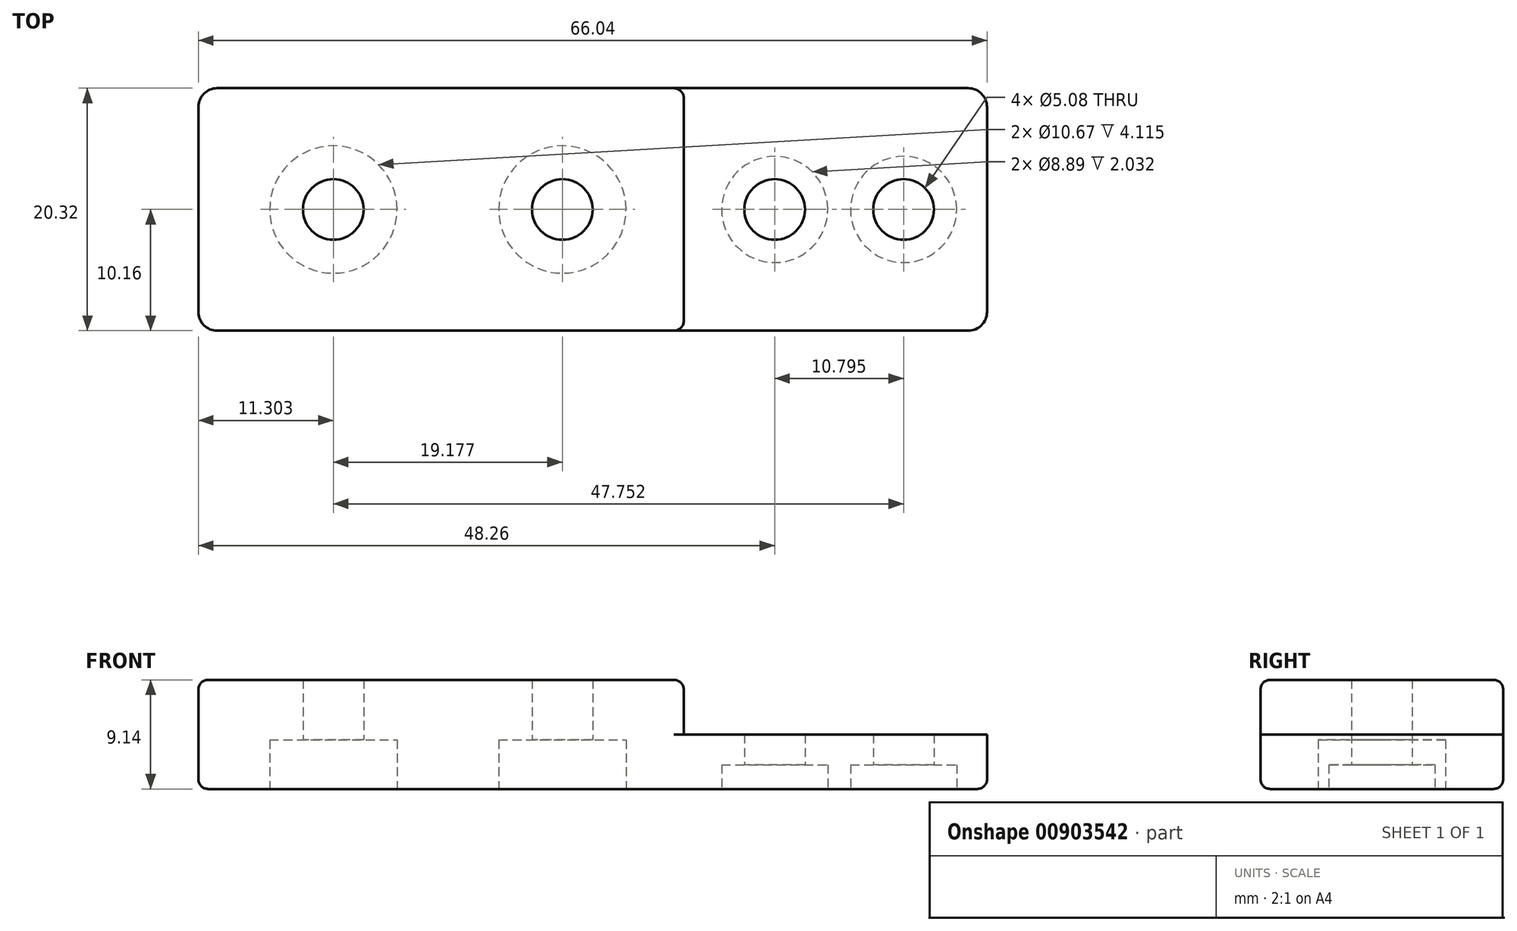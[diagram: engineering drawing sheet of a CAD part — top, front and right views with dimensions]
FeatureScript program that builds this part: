
annotation { "Feature Type Name" : "Feature", "Feature Type Description" : "" }
export const myFeature = defineFeature(function(context is Context, id is Id, definition is map)
    precondition{}
    {
        {
            var Q0;
            Q0=qCreatedBy(makeId("Top.planeOp"),FACE);
            var sketch = newSketch(context, id + "F0", { "sketchPlane" : qUnion([Q0])});
            skLineSegment(sketch, "E0.bottom", {"start": v(-40.64, 10.16) * mm, "end": v(0, 10.16) * mm});
            skLineSegment(sketch, "E0.top", {"start": v(-40.64, -10.16) * mm, "end": v(0, -10.16) * mm});
            skLineSegment(sketch, "E0.left", {"start": v(-40.64, 10.16) * mm, "end": v(-40.64, -10.16) * mm});
            skLineSegment(sketch, "E0.right", {"start": v(0, 10.16) * mm, "end": v(0, -10.16) * mm});
            skCircle(sketch, "E1", {"center": v(-29.34, 0) * mm, "radius": 2.54 * mm});
            skCircle(sketch, "E2", {"center": v(-10.16, 0) * mm, "radius": 2.54 * mm});
            skSolve(sketch);
        }
        {
            var Q0;
            Q0 = qSketchRegion(id + "F0", true);
            extrude(context, id + "F1", {"entities" : qUnion([Q0]), "depth" : 9.14 * mm, "offsetDistance" : 25.4 * mm});
        }
        {
            var Q0;
            Q0=qCreatedBy(makeId("Top.planeOp"),FACE);
            var sketch = newSketch(context, id + "F2", { "sketchPlane" : qUnion([Q0])});
            skLineSegment(sketch, "E3.bottom", {"start": v(0, 10.16) * mm, "end": v(25.4, 10.16) * mm});
            skLineSegment(sketch, "E3.top", {"start": v(0, -10.16) * mm, "end": v(25.4, -10.16) * mm});
            skLineSegment(sketch, "E3.left", {"start": v(0, 10.16) * mm, "end": v(0, -10.16) * mm});
            skLineSegment(sketch, "E3.right", {"start": v(25.4, 10.16) * mm, "end": v(25.4, -10.16) * mm});
            skCircle(sketch, "E4", {"center": v(7.62, 0) * mm, "radius": 2.54 * mm});
            skCircle(sketch, "E5", {"center": v(18.41, 0) * mm, "radius": 2.54 * mm});
            skSolve(sketch);
        }
        {
            var Q0;
            Q0 = qSketchRegion(id + "F2", true);
            extrude(context, id + "F3", {"entities" : qUnion([Q0]), "operationType" : NewBodyOperationType.ADD, "depth" : 4.57 * mm, "offsetDistance" : 25.4 * mm});
        }
        {
            var Q0;
            Q0=makeQuery(id+"F3.boolean.opBoolean","MERGE",FACE,{"derivedFrom":[makeQuery(id+"F1.opExtrude","CAP_FACE",FACE,{"disambiguationData":[OSD([sQuery(id+"F0.wireOp",EDGE,"E0.bottom"),sQuery(id+"F0.wireOp",EDGE,"E0.top"),sQuery(id+"F0.wireOp",EDGE,"E0.left"),sQuery(id+"F0.wireOp",EDGE,"E0.right"),sQuery(id+"F0.wireOp",EDGE,"E1"),sQuery(id+"F0.wireOp",EDGE,"E2")])],"isStart":true}),makeQuery(id+"F3.opExtrude","CAP_FACE",FACE,{"disambiguationData":[OSD([sQuery(id+"F2.wireOp",EDGE,"E3.bottom"),sQuery(id+"F2.wireOp",EDGE,"E3.top"),sQuery(id+"F2.wireOp",EDGE,"E3.left"),sQuery(id+"F2.wireOp",EDGE,"E3.right"),sQuery(id+"F2.wireOp",EDGE,"E4"),sQuery(id+"F2.wireOp",EDGE,"E5")])],"isStart":true})]});
            var sketch = newSketch(context, id + "F4", { "sketchPlane" : qUnion([Q0])});
            skCircle(sketch, "E6", {"center": v(-29.34, 0) * mm, "radius": 5.33 * mm});
            skCircle(sketch, "E7", {"center": v(-10.16, 0) * mm, "radius": 5.33 * mm});
            skCircle(sketch, "E8", {"center": v(-29.34, 0) * mm, "radius": 2.54 * mm});
            skCircle(sketch, "E9", {"center": v(-10.16, 0) * mm, "radius": 2.54 * mm});
            skSolve(sketch);
        }
        {
            var Q0;
            Q0 = qSketchRegion(id + "F4", true);
            extrude(context, id + "F5", {"entities" : qUnion([Q0]), "operationType" : NewBodyOperationType.REMOVE, "oppositeDirection" : true, "depth" : 4.11 * mm, "offsetDistance" : 25.4 * mm});
        }
        {
            var Q0;
            Q0=makeQuery(id+"F3.boolean.opBoolean","MERGE",FACE,{"derivedFrom":[makeQuery(id+"F1.opExtrude","CAP_FACE",FACE,{"disambiguationData":[OSD([sQuery(id+"F0.wireOp",EDGE,"E0.bottom"),sQuery(id+"F0.wireOp",EDGE,"E0.top"),sQuery(id+"F0.wireOp",EDGE,"E0.left"),sQuery(id+"F0.wireOp",EDGE,"E0.right"),sQuery(id+"F0.wireOp",EDGE,"E1"),sQuery(id+"F0.wireOp",EDGE,"E2")])],"isStart":true}),makeQuery(id+"F3.opExtrude","CAP_FACE",FACE,{"disambiguationData":[OSD([sQuery(id+"F2.wireOp",EDGE,"E3.bottom"),sQuery(id+"F2.wireOp",EDGE,"E3.top"),sQuery(id+"F2.wireOp",EDGE,"E3.left"),sQuery(id+"F2.wireOp",EDGE,"E3.right"),sQuery(id+"F2.wireOp",EDGE,"E4"),sQuery(id+"F2.wireOp",EDGE,"E5")])],"isStart":true})]});
            var sketch = newSketch(context, id + "F6", { "sketchPlane" : qUnion([Q0])});
            skCircle(sketch, "E10", {"center": v(7.62, 0) * mm, "radius": 4.45 * mm});
            skCircle(sketch, "E11", {"center": v(18.41, 0) * mm, "radius": 4.45 * mm});
            skCircle(sketch, "E12", {"center": v(7.62, 0) * mm, "radius": 2.54 * mm});
            skCircle(sketch, "E13", {"center": v(18.41, 0) * mm, "radius": 2.54 * mm});
            skSolve(sketch);
        }
        {
            var Q0;
            Q0 = qSketchRegion(id + "F6", true);
            extrude(context, id + "F7", {"entities" : qUnion([Q0]), "operationType" : NewBodyOperationType.REMOVE, "oppositeDirection" : true, "depth" : 2.03 * mm, "offsetDistance" : 25.4 * mm});
        }
        {
            var Q0;
            Q0=makeQuery(id+"F1.opExtrude","SWEPT_EDGE",EDGE,{"disambiguationData":[OSD([sQuery(id+"F0.wireOp",EDGE,"E0.bottom"),sQuery(id+"F0.wireOp",EDGE,"E0.left")])]});
            var Q1;
            Q1=makeQuery(id+"F1.opExtrude","SWEPT_EDGE",EDGE,{"disambiguationData":[OSD([sQuery(id+"F0.wireOp",EDGE,"E0.top"),sQuery(id+"F0.wireOp",EDGE,"E0.left")])]});
            var Q2;
            Q2=makeQuery(id+"F3.opExtrude","SWEPT_EDGE",EDGE,{"disambiguationData":[OSD([sQuery(id+"F2.wireOp",EDGE,"E3.bottom"),sQuery(id+"F2.wireOp",EDGE,"E3.right")])]});
            var Q3;
            Q3=makeQuery(id+"F3.opExtrude","SWEPT_EDGE",EDGE,{"disambiguationData":[OSD([sQuery(id+"F2.wireOp",EDGE,"E3.top"),sQuery(id+"F2.wireOp",EDGE,"E3.right")])]});
            fillet(context, id + "F8", {"entities" : qUnion([Q0, Q1, Q2, Q3]), "radius" : 1.57 * mm, "tangentPropagation" : true, "allowEdgeOverflow" : false});
        }
        {
            var Q0;
            Q0=makeQuery(id+"F3.opExtrude","CAP_EDGE",EDGE,{"disambiguationData":[OSD([sQuery(id+"F2.wireOp",EDGE,"E3.left")])],"isStart":false});
            var Q1;
            Q1=makeQuery(id+"F1.opExtrude","SWEPT_EDGE",EDGE,{"disambiguationData":[OSD([sQuery(id+"F0.wireOp",EDGE,"E0.bottom"),sQuery(id+"F0.wireOp",EDGE,"E0.right")])]});
            var Q2;
            Q2=makeQuery(id+"F1.opExtrude","CAP_EDGE",EDGE,{"disambiguationData":[OSD([sQuery(id+"F0.wireOp",EDGE,"E0.right")])],"isStart":false});
            fillet(context, id + "F9", {"entities" : qUnion([Q0, Q1, Q2]), "radius" : 0.81 * mm, "tangentPropagation" : true, "allowEdgeOverflow" : false});
        }
        {
            var Q0;
            Q0=makeQuery(id+"F1.opExtrude","CAP_EDGE",EDGE,{"disambiguationData":[OSD([sQuery(id+"F0.wireOp",EDGE,"E0.top")])],"isStart":false});
            var Q1;
            Q1=makeQuery(id+"F3.boolean.opBoolean","MERGE",EDGE,{"derivedFrom":[makeQuery(id+"F1.opExtrude","CAP_EDGE",EDGE,{"disambiguationData":[OSD([sQuery(id+"F0.wireOp",EDGE,"E0.bottom")])],"isStart":true}),makeQuery(id+"F3.opExtrude","CAP_EDGE",EDGE,{"disambiguationData":[OSD([sQuery(id+"F2.wireOp",EDGE,"E3.bottom")])],"isStart":true})]});
            fillet(context, id + "F10", {"entities" : qUnion([Q0, Q1]), "radius" : 0.81 * mm, "tangentPropagation" : true, "allowEdgeOverflow" : false});
        }
    });
